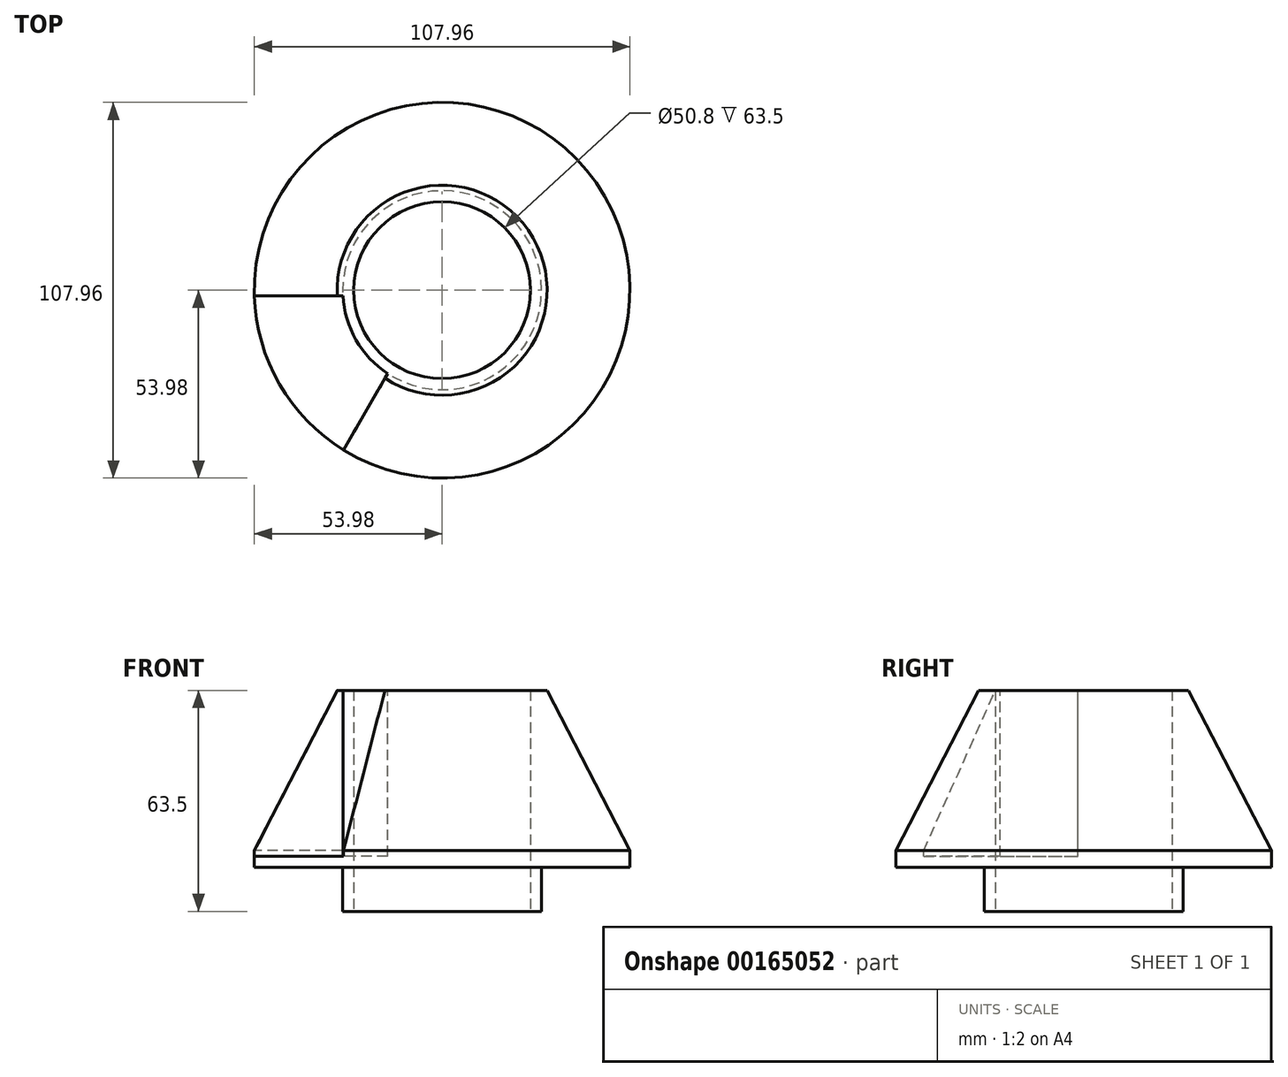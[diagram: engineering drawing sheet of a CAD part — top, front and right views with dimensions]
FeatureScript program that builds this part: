
annotation { "Feature Type Name" : "Feature", "Feature Type Description" : "" }
export const myFeature = defineFeature(function(context is Context, id is Id, definition is map)
    precondition{}
    {
        {
            var Q0;
            Q0=qCreatedBy(makeId("Top.planeOp"),FACE);
            var sketch = newSketch(context, id + "F0", { "sketchPlane" : qUnion([Q0])});
            skCircle(sketch, "E0", {"center": v(0, 0) * mm, "radius": 25.4 * mm});
            skCircle(sketch, "E1", {"center": v(0, 0) * mm, "radius": 28.58 * mm});
            skSolve(sketch);
        }
        {
            var Q0;
            Q0 = qSketchRegion(id + "F0", true);
            extrude(context, id + "F1", {"entities" : qUnion([Q0]), "depth" : 12.7 * mm});
        }
        {
            var Q0;
            Q0=makeQuery(id+"F1.opExtrude","CAP_FACE",FACE,{"disambiguationData":[OSD([sQuery(id+"F0.wireOp",EDGE,"E0"),sQuery(id+"F0.wireOp",EDGE,"E1")])],"isStart":false});
            var sketch = newSketch(context, id + "F2", { "sketchPlane" : qUnion([Q0])});
            skCircle(sketch, "E2", {"center": v(0, 0) * mm, "radius": 53.98 * mm});
            skCircle(sketch, "E3", {"center": v(0, 0) * mm, "radius": 25.4 * mm});
            skSolve(sketch);
        }
        {
            var Q0;
            Q0 = qSketchRegion(id + "F2", true);
            extrude(context, id + "F3", {"entities" : qUnion([Q0]), "operationType" : NewBodyOperationType.ADD, "depth" : 50.8 * mm});
        }
        {
            var Q0;
            Q0=makeQuery(id+"F3.opExtrude","CAP_FACE",FACE,{"disambiguationData":[OSD([sQuery(id+"F2.wireOp",EDGE,"E2"),sQuery(id+"F2.wireOp",EDGE,"E3")])],"isStart":true});
            cPlane(context, id + "F4", {"entities" : qUnion([Q0]), "cplaneType" : CPlaneType.OFFSET, "offset" : 3.17 * mm, "oppositeDirection" : true, "width" : 152.4 * mm, "height" : 152.4 * mm});
        }
        {
            var Q0;
            Q0=makeQuery(id+"F3.opExtrude","CAP_FACE",FACE,{"disambiguationData":[OSD([sQuery(id+"F2.wireOp",EDGE,"E2"),sQuery(id+"F2.wireOp",EDGE,"E3")])],"isStart":false});
            var sketch = newSketch(context, id + "F5", { "sketchPlane" : qUnion([Q0])});
            skArc(sketch, "E4", {"start": v(-28.53, -1.59) * mm, "mid": v(-24.75, -14.29) * mm, "end": v(-15.64, -23.91) * mm});
            skArc(sketch, "E5", {"start": v(-53.95, -1.59) * mm, "mid": v(-46.74, -26.99) * mm, "end": v(-28.35, -45.93) * mm});
            skLineSegment(sketch, "E6", {"start": v(-28.53, -1.59) * mm, "end": v(-53.95, -1.59) * mm});
            skLineSegment(sketch, "E7", {"start": v(-15.64, -23.91) * mm, "end": v(-28.35, -45.93) * mm});
            skLineSegment(sketch, "E8", {"start": v(0, 0) * mm, "end": v(-41.24, 0) * mm, "construction": true});
            skLineSegment(sketch, "E9", {"start": v(-41.24, 0) * mm, "end": v(-41.24, -1.59) * mm, "construction": true});
            skLineSegment(sketch, "E10", {"start": v(0, 0) * mm, "end": v(-20.62, -35.72) * mm, "construction": true});
            skLineSegment(sketch, "E11", {"start": v(-20.62, -35.72) * mm, "end": v(-22, -34.92) * mm, "construction": true});
            skSolve(sketch);
        }
        {
            var Q0;
            Q0 = qSketchRegion(id + "F5", true);
            var Q1;
            Q1=qCreatedBy(id+"F4.planeOp",FACE);
            extrude(context, id + "F6", {"entities" : qUnion([Q0]), "operationType" : NewBodyOperationType.REMOVE, "endBound" : BoundingType.UP_TO_SURFACE, "oppositeDirection" : true, "endBoundEntityFace" : qUnion([Q1]), "depth" : 25.4 * mm});
        }
        {
            var Q0;
            Q0=qCreatedBy(makeId("Front.planeOp"),FACE);
            var sketch = newSketch(context, id + "F7", { "sketchPlane" : qUnion([Q0])});
            skLineSegment(sketch, "E12.bottom", {"start": v(-30.16, 63.5) * mm, "end": v(-53.98, 63.5) * mm});
            skLineSegment(sketch, "E12.top", {"start": v(-30.16, 17.46) * mm, "end": v(-53.97, 17.46) * mm, "construction": true});
            skLineSegment(sketch, "E12.left", {"start": v(-30.16, 63.5) * mm, "end": v(-30.16, 17.46) * mm, "construction": true});
            skLineSegment(sketch, "E12.right", {"start": v(-53.98, 63.5) * mm, "end": v(-53.97, 17.46) * mm});
            skLineSegment(sketch, "E13", {"start": v(-30.16, 63.5) * mm, "end": v(0, 63.5) * mm, "construction": true});
            skLineSegment(sketch, "E14", {"start": v(-53.97, 17.46) * mm, "end": v(-53.97, 15.87) * mm, "construction": true});
            skLineSegment(sketch, "E15", {"start": v(-30.16, 63.5) * mm, "end": v(-53.97, 17.46) * mm});
            skSolve(sketch);
        }
        {
            var Q0;
            Q0 = qSketchRegion(id + "F7", true);
            var Q1;
            Q1=makeQuery(id+"F3.boolean.opBoolean","MERGE",FACE,{"derivedFrom":[makeQuery(id+"F1.opExtrude","SWEPT_FACE",FACE,{"disambiguationData":[OSD([sQuery(id+"F0.wireOp",EDGE,"E0")])]}),makeQuery(id+"F3.opExtrude","SWEPT_FACE",FACE,{"disambiguationData":[OSD([sQuery(id+"F2.wireOp",EDGE,"E3")])]})]});
            revolve(context, id + "F8", {"operationType" : NewBodyOperationType.REMOVE, "entities" : qUnion([Q0]), "axis" : qUnion([Q1]), "revolveType" : RevolveType.FULL, "oppositeDirection" : true});
        }
    });
